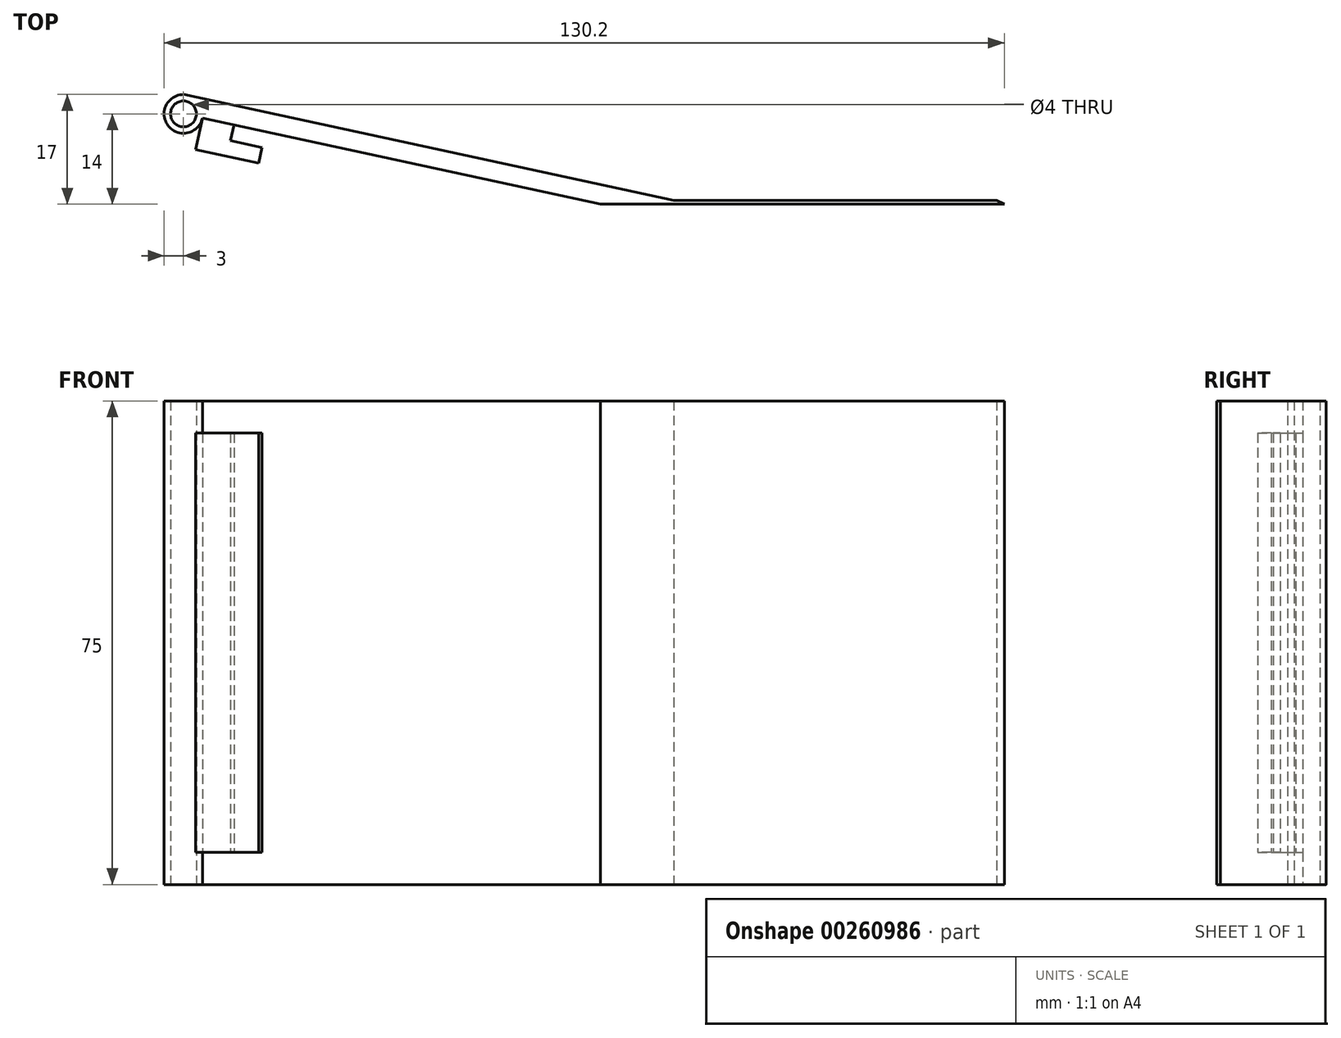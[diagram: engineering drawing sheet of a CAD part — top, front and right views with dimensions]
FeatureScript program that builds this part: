
annotation { "Feature Type Name" : "Feature", "Feature Type Description" : "" }
export const myFeature = defineFeature(function(context is Context, id is Id, definition is map)
    precondition{}
    {
        {
            var Q0;
            Q0=qCreatedBy(makeId("Top.planeOp"),FACE);
            var sketch = newSketch(context, id + "F0", { "sketchPlane" : qUnion([Q0])});
            skCircle(sketch, "E0", {"center": v(-1, 14) * mm, "radius": 2 * mm});
            skArc(sketch, "E1", {"start": v(-0.36, 16.93) * mm, "mid": v(-3.97, 13.6) * mm, "end": v(0.37, 11.33) * mm});
            skLineSegment(sketch, "E2", {"start": v(75, 0) * mm, "end": v(76.2, 0) * mm});
            skLineSegment(sketch, "E3", {"start": v(75, 0.6) * mm, "end": v(-0.36, 16.93) * mm});
            skLineSegment(sketch, "E4", {"start": v(1.93, 13.36) * mm, "end": v(63.6, 0) * mm});
            skArc(sketch, "E5", {"start": v(-0.36, 16.93) * mm, "mid": v(-3.52, 12.38) * mm, "end": v(1.93, 13.36) * mm});
            skLineSegment(sketch, "E6", {"start": v(75, 0) * mm, "end": v(125, 0) * mm});
            skLineSegment(sketch, "E7", {"start": v(125, 0.6) * mm, "end": v(75, 0.6) * mm});
            skLineSegment(sketch, "E8", {"start": v(63.6, 0) * mm, "end": v(75, 0) * mm});
            skLineSegment(sketch, "E9", {"start": v(125, 0) * mm, "end": v(126.2, 0) * mm});
            skLineSegment(sketch, "E10", {"start": v(126.2, 0) * mm, "end": v(125, 0.6) * mm});
            skSolve(sketch);
        }
        {
            var Q0;
            Q0=makeQuery(id+"F0.imprint","IMPRINT",FACE,{"disambiguationData":[TD([[makeQuery(id+"F0.imprint","IMPRINT",EDGE,{"derivedFrom":sQuery(id+"F0.wireOp",EDGE,"E0")}),-1.0]])]});
            extrude(context, id + "F1", {"entities" : qUnion([Q0]), "depth" : 75 * mm});
        }
        {
            var Q0;
            Q0=makeQuery(id+"F1.opExtrude","SWEPT_FACE",FACE,{"disambiguationData":[OSD([sQuery(id+"F0.wireOp",EDGE,"E4")])]});
            var sketch = newSketch(context, id + "F2", { "sketchPlane" : qUnion([Q0])});
            skLineSegment(sketch, "E11.0", {"start": v(-0.94, 75) * mm, "end": v(-0.94, 0) * mm, "construction": true});
            skLineSegment(sketch, "E12.0", {"start": v(-0.94, 75) * mm, "end": v(62.16, 75) * mm, "construction": true});
            skLineSegment(sketch, "E13.0", {"start": v(-0.94, 0) * mm, "end": v(62.16, 0) * mm, "construction": true});
            skLineSegment(sketch, "E14", {"start": v(-0.94, 75) * mm, "end": v(1.89, 75) * mm, "construction": true});
            skLineSegment(sketch, "E15", {"start": v(-0.94, 75) * mm, "end": v(9.06, 75) * mm});
            skLineSegment(sketch, "E16", {"start": v(9.06, 75) * mm, "end": v(9.06, 0) * mm});
            skLineSegment(sketch, "E17", {"start": v(9.06, 0) * mm, "end": v(-0.94, 0) * mm});
            skSolve(sketch);
        }
        {
            var Q0;
            Q0=makeQuery(id+"F2.imprint","IMPRINT",FACE,{"disambiguationData":[TD([[makeQuery(id+"F2.imprint","IMPRINT",EDGE,{"derivedFrom":sQuery(id+"F2.wireOp",EDGE,"E15")}),-1.0]])]});
            extrude(context, id + "F3", {"entities" : qUnion([Q0]), "operationType" : NewBodyOperationType.ADD, "depth" : 5 * mm});
        }
        {
            var Q0;
            Q0=makeQuery(id+"F3.opExtrude","SWEPT_FACE",FACE,{"disambiguationData":[OSD([sQuery(id+"F2.wireOp",EDGE,"E16")])]});
            var sketch = newSketch(context, id + "F4", { "sketchPlane" : qUnion([Q0])});
            skLineSegment(sketch, "E18", {"start": v(10.97, 75) * mm, "end": v(10.97, 0) * mm});
            skLineSegment(sketch, "E19.0", {"start": v(8.47, 75) * mm, "end": v(13.47, 75) * mm});
            skLineSegment(sketch, "E20.0", {"start": v(13.47, 75) * mm, "end": v(13.47, 0) * mm});
            skLineSegment(sketch, "E21.0", {"start": v(8.47, 0) * mm, "end": v(13.47, 0) * mm});
            skSolve(sketch);
        }
        {
            var Q0;
            {var subQ0=sQuery(id+"F4.wireOp",EDGE,"E18");Q0=makeQuery(id+"F4.imprint","IMPRINT",FACE,{"disambiguationData":[TD([[makeQuery(id+"F4.imprint","IMPRINT",EDGE,{"derivedFrom":subQ0}),1.0]])]});}
            extrude(context, id + "F5", {"entities" : qUnion([Q0]), "operationType" : NewBodyOperationType.REMOVE, "oppositeDirection" : true, "depth" : 5 * mm});
        }
        {
            var Q0;
            Q0=makeQuery(id+"F3.boolean.opBoolean","MERGE",FACE,{"derivedFrom":[makeQuery(id+"F1.opExtrude","CAP_FACE",FACE,{"disambiguationData":[OSD([sQuery(id+"F0.wireOp",EDGE,"E0"),sQuery(id+"F0.wireOp",EDGE,"E3"),sQuery(id+"F0.wireOp",EDGE,"E4"),sQuery(id+"F0.wireOp",EDGE,"E5"),sQuery(id+"F0.wireOp",EDGE,"E6"),sQuery(id+"F0.wireOp",EDGE,"E7"),sQuery(id+"F0.wireOp",EDGE,"E8"),sQuery(id+"F0.wireOp",EDGE,"E9"),sQuery(id+"F0.wireOp",EDGE,"E10")])],"isStart":false}),makeQuery(id+"F3.opExtrude","SWEPT_FACE",FACE,{"disambiguationData":[OSD([sQuery(id+"F2.wireOp",EDGE,"E15")])]})]});
            var sketch = newSketch(context, id + "F6", { "sketchPlane" : qUnion([Q0])});
            skLineSegment(sketch, "E22", {"start": v(6.82, 12.3) * mm, "end": v(1.93, 13.36) * mm});
            skSolve(sketch);
        }
        {
            var Q0;
            Q0=makeQuery(id+"F6.imprint","IMPRINT",FACE,{"disambiguationData":[TD([[makeQuery(id+"F6.imprint","IMPRINT",EDGE,{"derivedFrom":sQuery(id+"F6.wireOp",EDGE,"E22")}),1.0]])]});
            extrude(context, id + "F7", {"entities" : qUnion([Q0]), "operationType" : NewBodyOperationType.REMOVE, "oppositeDirection" : true, "depth" : 5 * mm});
        }
        {
            var Q0;
            Q0=makeQuery(id+"F3.boolean.opBoolean","MERGE",FACE,{"derivedFrom":[makeQuery(id+"F1.opExtrude","CAP_FACE",FACE,{"disambiguationData":[OSD([sQuery(id+"F0.wireOp",EDGE,"E0"),sQuery(id+"F0.wireOp",EDGE,"E3"),sQuery(id+"F0.wireOp",EDGE,"E4"),sQuery(id+"F0.wireOp",EDGE,"E5"),sQuery(id+"F0.wireOp",EDGE,"E6"),sQuery(id+"F0.wireOp",EDGE,"E7"),sQuery(id+"F0.wireOp",EDGE,"E8"),sQuery(id+"F0.wireOp",EDGE,"E9"),sQuery(id+"F0.wireOp",EDGE,"E10")])],"isStart":true}),makeQuery(id+"F3.opExtrude","SWEPT_FACE",FACE,{"disambiguationData":[OSD([sQuery(id+"F2.wireOp",EDGE,"E17")])]})]});
            var sketch = newSketch(context, id + "F8", { "sketchPlane" : qUnion([Q0])});
            skLineSegment(sketch, "E23", {"start": v(6.82, -12.3) * mm, "end": v(1.93, -13.36) * mm});
            skSolve(sketch);
        }
        {
            var Q0;
            Q0=makeQuery(id+"F8.imprint","IMPRINT",FACE,{"disambiguationData":[TD([[makeQuery(id+"F8.imprint","IMPRINT",EDGE,{"derivedFrom":sQuery(id+"F8.wireOp",EDGE,"E23")}),-1.0]])]});
            extrude(context, id + "F9", {"entities" : qUnion([Q0]), "operationType" : NewBodyOperationType.REMOVE, "oppositeDirection" : true, "depth" : 5 * mm});
        }
    });
